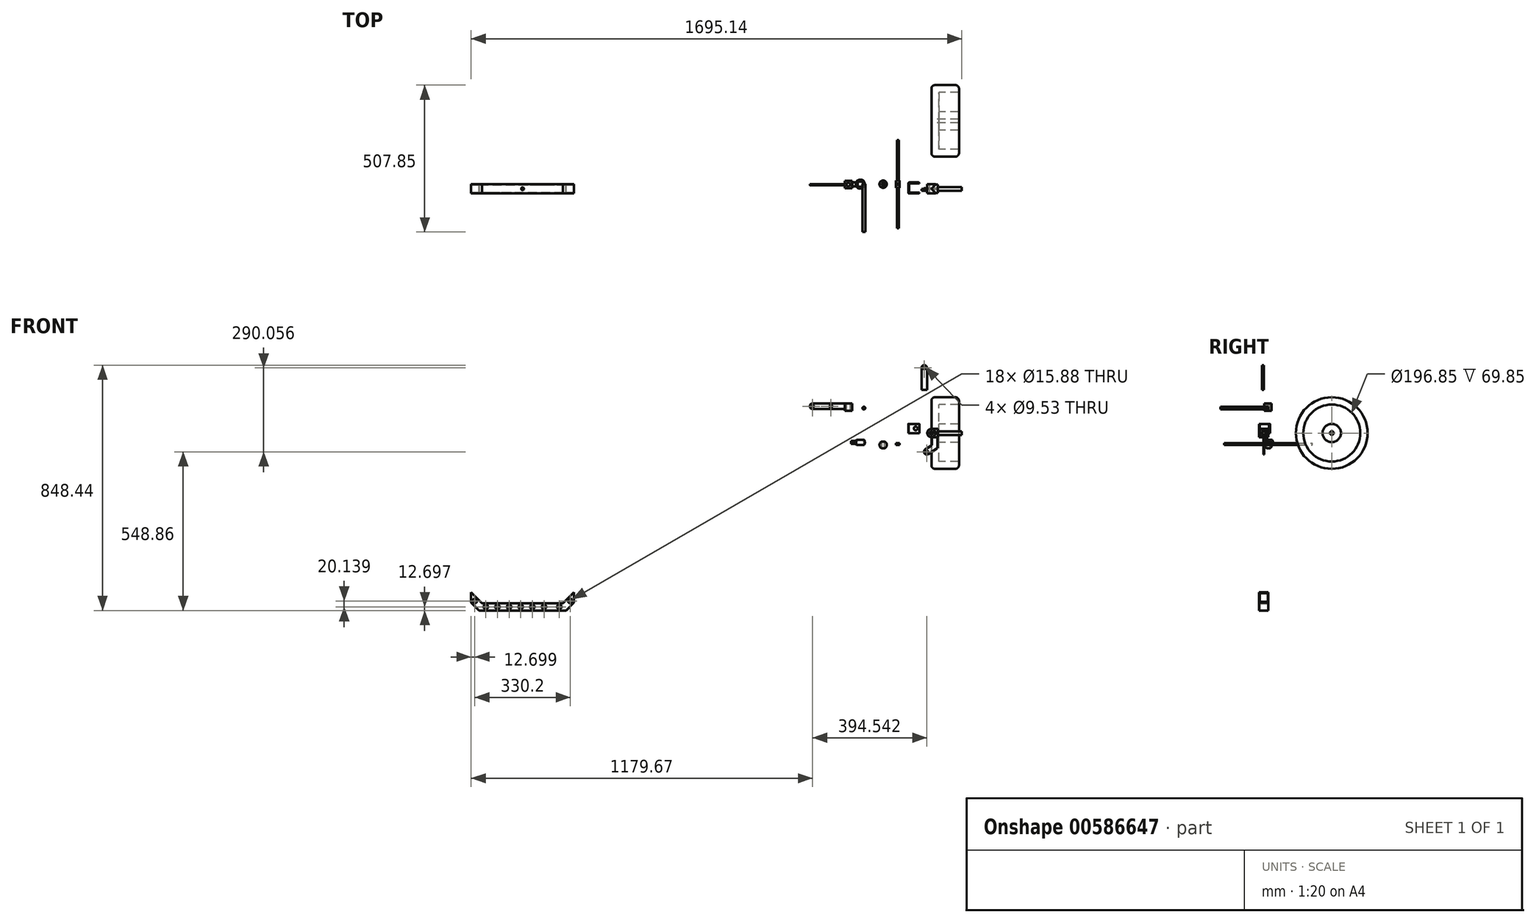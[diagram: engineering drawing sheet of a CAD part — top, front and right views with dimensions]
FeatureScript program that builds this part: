
annotation { "Feature Type Name" : "Feature", "Feature Type Description" : "" }
export const myFeature = defineFeature(function(context is Context, id is Id, definition is map)
    precondition{}
    {
        {
            var Q0;
            Q0=qCreatedBy(makeId("Front.planeOp"),FACE);
            var sketch = newSketch(context, id + "F0", { "sketchPlane" : qUnion([Q0])});
            skCircle(sketch, "E0", {"center": v(0, 0) * mm, "radius": 14.29 * mm});
            skCircle(sketch, "E1", {"center": v(0, 0) * mm, "radius": 6.35 * mm});
            skSolve(sketch);
        }
        {
            var Q0;
            Q0=makeQuery(id+"F0.imprint","IMPRINT",FACE,{"disambiguationData":[TD([[makeQuery(id+"F0.imprint","IMPRINT",EDGE,{"derivedFrom":sQuery(id+"F0.wireOp",EDGE,"E0")}),1.0]])]});
            extrude(context, id + "F1", {"entities" : qUnion([Q0]), "depth" : 31.75 * mm, "offsetDistance" : 25.4 * mm});
        }
        {
            var Q0;
            Q0=qCreatedBy(makeId("Right.planeOp"),FACE);
            cPlane(context, id + "F2", {"entities" : qUnion([Q0]), "cplaneType" : CPlaneType.OFFSET, "offset" : 22.22 * mm, "width" : 152.4 * mm, "height" : 152.4 * mm});
        }
        {
            var Q0;
            Q0=qCreatedBy(id+"F2.planeOp",FACE);
            var sketch = newSketch(context, id + "F3", { "sketchPlane" : qUnion([Q0])});
            skCircle(sketch, "E2", {"center": v(-15.88, 0) * mm, "radius": 14.29 * mm});
            skSolve(sketch);
        }
        {
            var Q0;
            Q0=makeQuery(id+"F3.imprint","IMPRINT",FACE,{"disambiguationData":[TD([[makeQuery(id+"F3.imprint","IMPRINT",EDGE,{"derivedFrom":sQuery(id+"F3.wireOp",EDGE,"E2")}),1.0]])]});
            extrude(context, id + "F4", {"entities" : qUnion([Q0]), "operationType" : NewBodyOperationType.ADD, "endBound" : BoundingType.UP_TO_NEXT, "oppositeDirection" : true, "depth" : 25.4 * mm, "offsetDistance" : 25.4 * mm});
        }
        {
            var Q0;
            Q0=makeQuery(id+"F4.opExtrude","CAP_FACE",FACE,{"disambiguationData":[OSD([sQuery(id+"F3.wireOp",EDGE,"E2")])],"isStart":true});
            var sketch = newSketch(context, id + "F5", { "sketchPlane" : qUnion([Q0])});
            skCircle(sketch, "E3", {"center": v(-15.88, 0) * mm, "radius": 6.35 * mm});
            skSolve(sketch);
        }
        {
            var Q0;
            Q0=makeQuery(id+"F5.imprint","IMPRINT",FACE,{"disambiguationData":[TD([[makeQuery(id+"F5.imprint","IMPRINT",EDGE,{"derivedFrom":sQuery(id+"F5.wireOp",EDGE,"E3")}),1.0]])]});
            extrude(context, id + "F6", {"entities" : qUnion([Q0]), "operationType" : NewBodyOperationType.ADD, "depth" : 82.55 * mm, "offsetDistance" : 25.4 * mm});
        }
        {
            var Q0;
            Q0=qCreatedBy(makeId("Top.planeOp"),FACE);
            var sketch = newSketch(context, id + "F7", { "sketchPlane" : qUnion([Q0])});
            skLineSegment(sketch, "E4.bottom", {"start": v(-76.48, 5.78) * mm, "end": v(-44.73, 5.78) * mm});
            skLineSegment(sketch, "E4.top", {"start": v(-76.48, -32.32) * mm, "end": v(-44.73, -32.32) * mm});
            skLineSegment(sketch, "E4.left", {"start": v(-79.65, 2.6) * mm, "end": v(-79.65, -29.15) * mm});
            skLineSegment(sketch, "E4.right", {"start": v(-41.55, 2.6) * mm, "end": v(-41.55, -29.15) * mm});
            skPoint(sketch, "E5.visualSharp", {"position": v(-41.55, 5.78) * mm});
            skArc(sketch, "E5.filletArc", {"start": v(-41.55, 2.6) * mm, "mid": v(-42.48, 4.85) * mm, "end": v(-44.73, 5.78) * mm});
            skPoint(sketch, "E6.visualSharp", {"position": v(-41.55, -32.32) * mm});
            skArc(sketch, "E6.filletArc", {"start": v(-44.73, -32.32) * mm, "mid": v(-42.48, -31.4) * mm, "end": v(-41.55, -29.15) * mm});
            skPoint(sketch, "E7.visualSharp", {"position": v(-79.65, -32.32) * mm});
            skArc(sketch, "E7.filletArc", {"start": v(-79.65, -29.15) * mm, "mid": v(-78.72, -31.4) * mm, "end": v(-76.48, -32.32) * mm});
            skPoint(sketch, "E8.visualSharp", {"position": v(-79.65, 5.78) * mm});
            skArc(sketch, "E8.filletArc", {"start": v(-76.48, 5.78) * mm, "mid": v(-78.72, 4.85) * mm, "end": v(-79.65, 2.6) * mm});
            skLineSegment(sketch, "E9.0", {"start": v(-76.48, 2.73) * mm, "end": v(-44.73, 2.73) * mm});
            skArc(sketch, "E9.1", {"start": v(-44.6, 2.6) * mm, "mid": v(-44.64, 2.7) * mm, "end": v(-44.73, 2.73) * mm});
            skArc(sketch, "E9.2", {"start": v(-76.48, 2.73) * mm, "mid": v(-76.57, 2.7) * mm, "end": v(-76.6, 2.6) * mm});
            skLineSegment(sketch, "E9.3", {"start": v(-44.6, 2.6) * mm, "end": v(-44.6, -29.15) * mm});
            skLineSegment(sketch, "E9.4", {"start": v(-76.6, 2.6) * mm, "end": v(-76.6, -29.15) * mm});
            skArc(sketch, "E9.5", {"start": v(-76.6, -29.15) * mm, "mid": v(-76.57, -29.24) * mm, "end": v(-76.48, -29.28) * mm});
            skLineSegment(sketch, "E9.6", {"start": v(-76.48, -29.28) * mm, "end": v(-44.73, -29.28) * mm});
            skArc(sketch, "E9.7", {"start": v(-44.73, -29.28) * mm, "mid": v(-44.64, -29.24) * mm, "end": v(-44.6, -29.15) * mm});
            skSolve(sketch);
        }
        {
            var Q0;
            Q0=makeQuery(id+"F7.imprint","IMPRINT",FACE,{"disambiguationData":[TD([[makeQuery(id+"F7.imprint","IMPRINT",EDGE,{"derivedFrom":sQuery(id+"F7.wireOp",EDGE,"E4.bottom")}),-1.0]])]});
            extrude(context, id + "F8", {"entities" : qUnion([Q0]), "depth" : 31.75 * mm, "offsetDistance" : 25.4 * mm});
        }
        {
            var Q0;
            Q0=makeQuery(id+"F8.opExtrude","CAP_FACE",FACE,{"disambiguationData":[OSD([sQuery(id+"F7.wireOp",EDGE,"E4.bottom"),sQuery(id+"F7.wireOp",EDGE,"E4.top"),sQuery(id+"F7.wireOp",EDGE,"E4.left"),sQuery(id+"F7.wireOp",EDGE,"E4.right"),sQuery(id+"F7.wireOp",EDGE,"E5.filletArc"),sQuery(id+"F7.wireOp",EDGE,"E6.filletArc"),sQuery(id+"F7.wireOp",EDGE,"E7.filletArc"),sQuery(id+"F7.wireOp",EDGE,"E8.filletArc"),sQuery(id+"F7.wireOp",EDGE,"E9.0"),sQuery(id+"F7.wireOp",EDGE,"E9.1"),sQuery(id+"F7.wireOp",EDGE,"E9.2"),sQuery(id+"F7.wireOp",EDGE,"E9.3"),sQuery(id+"F7.wireOp",EDGE,"E9.4"),sQuery(id+"F7.wireOp",EDGE,"E9.5"),sQuery(id+"F7.wireOp",EDGE,"E9.6"),sQuery(id+"F7.wireOp",EDGE,"E9.7")])],"isStart":false});
            var sketch = newSketch(context, id + "F9", { "sketchPlane" : qUnion([Q0])});
            skLineSegment(sketch, "E10.bottom", {"start": v(-44.73, 2.73) * mm, "end": v(-41.56, 2.73) * mm});
            skLineSegment(sketch, "E10.top", {"start": v(-44.73, -29.28) * mm, "end": v(-41.56, -29.28) * mm});
            skLineSegment(sketch, "E10.left", {"start": v(-44.73, 2.73) * mm, "end": v(-44.73, -29.28) * mm});
            skLineSegment(sketch, "E10.right", {"start": v(-41.56, 2.73) * mm, "end": v(-41.56, -29.28) * mm});
            skSolve(sketch);
        }
        {
            var Q0;
            Q0=makeQuery(id+"F9.imprint","IMPRINT",FACE,{"disambiguationData":[TD([[makeQuery(id+"F9.imprint","IMPRINT",EDGE,{"derivedFrom":sQuery(id+"F9.wireOp",EDGE,"E10.bottom")}),-1.0]])]});
            extrude(context, id + "F10", {"entities" : qUnion([Q0]), "operationType" : NewBodyOperationType.REMOVE, "endBound" : BoundingType.UP_TO_NEXT, "oppositeDirection" : true, "depth" : 25.4 * mm, "offsetDistance" : 25.4 * mm});
        }
        {
            var Q0;
            Q0=makeQuery(id+"F8.opExtrude","SWEPT_FACE",FACE,{"disambiguationData":[OSD([sQuery(id+"F7.wireOp",EDGE,"E4.bottom")])]});
            var sketch = newSketch(context, id + "F11", { "sketchPlane" : qUnion([Q0])});
            skCircle(sketch, "E11", {"center": v(54.26, 15.87) * mm, "radius": 6.35 * mm});
            skSolve(sketch);
        }
        {
            var Q0;
            Q0=makeQuery(id+"F11.imprint","IMPRINT",FACE,{"disambiguationData":[TD([[makeQuery(id+"F11.imprint","IMPRINT",EDGE,{"derivedFrom":sQuery(id+"F11.wireOp",EDGE,"E11")}),1.0]])]});
            var Q1;
            Q1=makeQuery(id+"F8.opExtrude","SWEPT_FACE",FACE,{"disambiguationData":[OSD([sQuery(id+"F7.wireOp",EDGE,"E4.top")])]});
            extrude(context, id + "F12", {"entities" : qUnion([Q0]), "operationType" : NewBodyOperationType.REMOVE, "endBound" : BoundingType.UP_TO_SURFACE, "oppositeDirection" : true, "depth" : 25.4 * mm, "endBoundEntityFace" : qUnion([Q1]), "offsetDistance" : 25.4 * mm});
        }
        {
            var Q0;
            Q0=qCreatedBy(makeId("Right.planeOp"),FACE);
            var sketch = newSketch(context, id + "F13", { "sketchPlane" : qUnion([Q0])});
            skCircle(sketch, "E12", {"center": v(218.92, 0) * mm, "radius": 123.83 * mm});
            skCircle(sketch, "E13", {"center": v(218.92, 0) * mm, "radius": 6.35 * mm});
            skSolve(sketch);
        }
        {
            var Q0;
            Q0=makeQuery(id+"F13.imprint","IMPRINT",FACE,{"disambiguationData":[TD([[makeQuery(id+"F13.imprint","IMPRINT",EDGE,{"derivedFrom":sQuery(id+"F13.wireOp",EDGE,"E12")}),1.0]])]});
            extrude(context, id + "F14", {"entities" : qUnion([Q0]), "depth" : 95.25 * mm, "offsetDistance" : 25.4 * mm});
        }
        {
            var Q0;
            Q0=makeQuery(id+"F14.opExtrude","CAP_EDGE",EDGE,{"disambiguationData":[OSD([sQuery(id+"F13.wireOp",EDGE,"E12")])],"isStart":false});
            var Q1;
            Q1=makeQuery(id+"F14.opExtrude","CAP_EDGE",EDGE,{"disambiguationData":[OSD([sQuery(id+"F13.wireOp",EDGE,"E12")])],"isStart":true});
            fillet(context, id + "F15", {"entities" : qUnion([Q0, Q1]), "radius" : 12.7 * mm, "tangentPropagation" : true, "allowEdgeOverflow" : false});
        }
        {
            var Q0;
            Q0=qCreatedBy(makeId("Front.planeOp"),FACE);
            cPlane(context, id + "F16", {"entities" : qUnion([Q0]), "cplaneType" : CPlaneType.OFFSET, "offset" : 15.88 * mm, "width" : 152.4 * mm, "height" : 152.4 * mm});
        }
        {
            var Q0;
            Q0=qCreatedBy(id+"F16.planeOp",FACE);
            var sketch = newSketch(context, id + "F17", { "sketchPlane" : qUnion([Q0])});
            skLineSegment(sketch, "E14", {"start": v(1.9, -13.97) * mm, "end": v(20.96, -13.97) * mm});
            skLineSegment(sketch, "E15", {"start": v(20.95, -13.97) * mm, "end": v(20.96, -52.07) * mm});
            skLineSegment(sketch, "E16", {"start": v(1.9, -13.97) * mm, "end": v(1.9, -41.72) * mm});
            skLineSegment(sketch, "E17", {"start": v(1.9, -41.72) * mm, "end": v(-21.33, -56.78) * mm});
            skLineSegment(sketch, "E18", {"start": v(20.96, -52.07) * mm, "end": v(-10.97, -72.76) * mm});
            skArc(sketch, "E19", {"start": v(-21.33, -56.78) * mm, "mid": v(-24.14, -69.95) * mm, "end": v(-10.97, -72.76) * mm});
            skCircle(sketch, "E20", {"center": v(-16.15, -64.77) * mm, "radius": 4.76 * mm});
            skLineSegment(sketch, "E21", {"start": v(0, 0) * mm, "end": v(-16.15, -64.77) * mm, "construction": true});
            skSolve(sketch);
        }
        {
            var Q0;
            Q0=makeQuery(id+"F17.imprint","IMPRINT",FACE,{"disambiguationData":[TD([[makeQuery(id+"F17.imprint","IMPRINT",EDGE,{"derivedFrom":sQuery(id+"F17.wireOp",EDGE,"E14")}),-1.0]])]});
            extrude(context, id + "F18", {"entities" : qUnion([Q0]), "operationType" : NewBodyOperationType.ADD, "depth" : 3.18 * mm, "offsetDistance" : 25.4 * mm, "symmetric" : true});
        }
        {
            var Q0;
            Q0=makeQuery(id+"F18.opExtrude","SWEPT_EDGE",EDGE,{"disambiguationData":[OSD([sQuery(id+"F17.wireOp",EDGE,"E15"),sQuery(id+"F17.wireOp",EDGE,"E18")])]});
            var Q1;
            Q1=makeQuery(id+"F18.opExtrude","SWEPT_EDGE",EDGE,{"disambiguationData":[OSD([sQuery(id+"F17.wireOp",EDGE,"E16"),sQuery(id+"F17.wireOp",EDGE,"E17")])]});
            fillet(context, id + "F19", {"entities" : qUnion([Q0, Q1]), "radius" : 6.35 * mm, "tangentPropagation" : true, "allowEdgeOverflow" : false});
        }
        {
            var Q0;
            Q0=qCreatedBy(makeId("Front.planeOp"),FACE);
            var sketch = newSketch(context, id + "F20", { "sketchPlane" : qUnion([Q0])});
            skLineSegment(sketch, "E22", {"start": v(-1590.36, -586.05) * mm, "end": v(-1562.78, -613.63) * mm});
            skLineSegment(sketch, "E23", {"start": v(-1562.78, -613.63) * mm, "end": v(-1262.34, -613.63) * mm});
            skLineSegment(sketch, "E24", {"start": v(-1262.34, -613.63) * mm, "end": v(-1234.76, -586.05) * mm});
            skLineSegment(sketch, "E25", {"start": v(-1234.76, -550.13) * mm, "end": v(-1272.86, -588.23) * mm});
            skLineSegment(sketch, "E26", {"start": v(-1272.86, -588.23) * mm, "end": v(-1552.26, -588.23) * mm});
            skLineSegment(sketch, "E27", {"start": v(-1552.26, -588.23) * mm, "end": v(-1590.36, -550.13) * mm});
            skLineSegment(sketch, "E28", {"start": v(-1590.36, -586.05) * mm, "end": v(-1590.36, -550.13) * mm});
            skLineSegment(sketch, "E29", {"start": v(-1234.76, -586.05) * mm, "end": v(-1234.76, -550.13) * mm});
            skSolve(sketch);
        }
        {
            var Q0;
            Q0=makeQuery(id+"F20.imprint","IMPRINT",FACE,{"disambiguationData":[TD([[makeQuery(id+"F20.imprint","IMPRINT",EDGE,{"derivedFrom":sQuery(id+"F20.wireOp",EDGE,"E22")}),1.0]])]});
            extrude(context, id + "F21", {"entities" : qUnion([Q0]), "depth" : 31.75 * mm, "offsetDistance" : 25.4 * mm});
        }
        {
            var Q0;
            Q0=makeQuery(id+"F21.opExtrude","SWEPT_FACE",FACE,{"disambiguationData":[OSD([sQuery(id+"F20.wireOp",EDGE,"E29")])]});
            shell(context, id + "F22", {"entities" : qUnion([Q0]), "thickness" : 2.1 * mm});
        }
        {
            var Q0;
            Q0=makeQuery(id+"F21.opExtrude","CAP_FACE",FACE,{"disambiguationData":[OSD([sQuery(id+"F20.wireOp",EDGE,"E22"),sQuery(id+"F20.wireOp",EDGE,"E23"),sQuery(id+"F20.wireOp",EDGE,"E24"),sQuery(id+"F20.wireOp",EDGE,"E25"),sQuery(id+"F20.wireOp",EDGE,"E26"),sQuery(id+"F20.wireOp",EDGE,"E27"),sQuery(id+"F20.wireOp",EDGE,"E28"),sQuery(id+"F20.wireOp",EDGE,"E29")])],"isStart":false});
            var sketch = newSketch(context, id + "F23", { "sketchPlane" : qUnion([Q0])});
            skCircle(sketch, "E30", {"center": v(-1577.66, -580.8) * mm, "radius": 7.94 * mm});
            skCircle(sketch, "E31", {"center": v(-1539.56, -600.93) * mm, "radius": 7.94 * mm});
            skCircle(sketch, "E32", {"center": v(-1499.35, -600.93) * mm, "radius": 7.94 * mm});
            skCircle(sketch, "E33", {"center": v(-1459.14, -600.93) * mm, "radius": 7.94 * mm});
            skCircle(sketch, "E34", {"center": v(-1418.94, -600.93) * mm, "radius": 7.94 * mm});
            skCircle(sketch, "E35", {"center": v(-1378.73, -600.93) * mm, "radius": 7.94 * mm});
            skCircle(sketch, "E36", {"center": v(-1338.52, -600.93) * mm, "radius": 7.94 * mm});
            skCircle(sketch, "E37", {"center": v(-1285.56, -600.93) * mm, "radius": 7.94 * mm});
            skCircle(sketch, "E38", {"center": v(-1247.46, -580.8) * mm, "radius": 7.94 * mm});
            skLineSegment(sketch, "E39", {"start": v(-1539.56, -600.93) * mm, "end": v(-1285.56, -600.93) * mm, "construction": true});
            skSolve(sketch);
        }
        {
            var Q0;
            Q0=makeQuery(id+"F23.imprint","IMPRINT",FACE,{"disambiguationData":[TD([[makeQuery(id+"F23.imprint","IMPRINT",EDGE,{"derivedFrom":sQuery(id+"F23.wireOp",EDGE,"E30")}),1.0]])]});
            var Q1;
            Q1=makeQuery(id+"F23.imprint","IMPRINT",FACE,{"disambiguationData":[TD([[makeQuery(id+"F23.imprint","IMPRINT",EDGE,{"derivedFrom":sQuery(id+"F23.wireOp",EDGE,"E31")}),1.0]])]});
            var Q2;
            Q2=makeQuery(id+"F23.imprint","IMPRINT",FACE,{"disambiguationData":[TD([[makeQuery(id+"F23.imprint","IMPRINT",EDGE,{"derivedFrom":sQuery(id+"F23.wireOp",EDGE,"E32")}),1.0]])]});
            var Q3;
            Q3=makeQuery(id+"F23.imprint","IMPRINT",FACE,{"disambiguationData":[TD([[makeQuery(id+"F23.imprint","IMPRINT",EDGE,{"derivedFrom":sQuery(id+"F23.wireOp",EDGE,"E33")}),1.0]])]});
            var Q4;
            Q4=makeQuery(id+"F23.imprint","IMPRINT",FACE,{"disambiguationData":[TD([[makeQuery(id+"F23.imprint","IMPRINT",EDGE,{"derivedFrom":sQuery(id+"F23.wireOp",EDGE,"E34")}),1.0]])]});
            var Q5;
            Q5=makeQuery(id+"F23.imprint","IMPRINT",FACE,{"disambiguationData":[TD([[makeQuery(id+"F23.imprint","IMPRINT",EDGE,{"derivedFrom":sQuery(id+"F23.wireOp",EDGE,"E35")}),1.0]])]});
            var Q6;
            Q6=makeQuery(id+"F23.imprint","IMPRINT",FACE,{"disambiguationData":[TD([[makeQuery(id+"F23.imprint","IMPRINT",EDGE,{"derivedFrom":sQuery(id+"F23.wireOp",EDGE,"E36")}),1.0]])]});
            var Q7;
            Q7=makeQuery(id+"F23.imprint","IMPRINT",FACE,{"disambiguationData":[TD([[makeQuery(id+"F23.imprint","IMPRINT",EDGE,{"derivedFrom":sQuery(id+"F23.wireOp",EDGE,"E37")}),1.0]])]});
            var Q8;
            Q8=makeQuery(id+"F23.imprint","IMPRINT",FACE,{"disambiguationData":[TD([[makeQuery(id+"F23.imprint","IMPRINT",EDGE,{"derivedFrom":sQuery(id+"F23.wireOp",EDGE,"E38")}),1.0]])]});
            var Q9;
            Q9=makeQuery(id+"F21.opExtrude","CAP_FACE",FACE,{"disambiguationData":[OSD([sQuery(id+"F20.wireOp",EDGE,"E22"),sQuery(id+"F20.wireOp",EDGE,"E23"),sQuery(id+"F20.wireOp",EDGE,"E24"),sQuery(id+"F20.wireOp",EDGE,"E25"),sQuery(id+"F20.wireOp",EDGE,"E26"),sQuery(id+"F20.wireOp",EDGE,"E27"),sQuery(id+"F20.wireOp",EDGE,"E28"),sQuery(id+"F20.wireOp",EDGE,"E29")])],"isStart":true});
            extrude(context, id + "F24", {"entities" : qUnion([Q0, Q1, Q2, Q3, Q4, Q5, Q6, Q7, Q8]), "operationType" : NewBodyOperationType.REMOVE, "endBound" : BoundingType.UP_TO_SURFACE, "oppositeDirection" : true, "depth" : 25.4 * mm, "endBoundEntityFace" : qUnion([Q9]), "offsetDistance" : 25.4 * mm});
        }
        {
            var Q0;
            Q0=makeQuery(id+"F14.opExtrude","CAP_FACE",FACE,{"disambiguationData":[OSD([sQuery(id+"F13.wireOp",EDGE,"E12"),sQuery(id+"F13.wireOp",EDGE,"E13")])],"isStart":false});
            shell(context, id + "F25", {"entities" : qUnion([Q0]), "thickness" : 25.4 * mm});
        }
        {
            var Q0;
            Q0=qCreatedBy(makeId("Front.planeOp"),FACE);
            var sketch = newSketch(context, id + "F26", { "sketchPlane" : qUnion([Q0])});
            skLineSegment(sketch, "E40.bottom", {"start": v(-410.7, 102.22) * mm, "end": v(-283.7, 102.22) * mm});
            skLineSegment(sketch, "E40.top", {"start": v(-410.7, 83.17) * mm, "end": v(-283.7, 83.17) * mm});
            skLineSegment(sketch, "E40.left", {"start": v(-410.7, 102.22) * mm, "end": v(-410.7, 83.17) * mm, "construction": true});
            skLineSegment(sketch, "E40.right", {"start": v(-283.7, 102.22) * mm, "end": v(-283.7, 83.17) * mm, "construction": true});
            skArc(sketch, "E41", {"start": v(-410.7, 102.22) * mm, "mid": v(-420.22, 92.7) * mm, "end": v(-410.7, 83.17) * mm});
            skArc(sketch, "E42", {"start": v(-283.7, 83.17) * mm, "mid": v(-274.17, 92.7) * mm, "end": v(-283.7, 102.22) * mm});
            skCircle(sketch, "E43", {"center": v(-410.7, 92.7) * mm, "radius": 4.76 * mm});
            skCircle(sketch, "E44", {"center": v(-283.7, 92.7) * mm, "radius": 4.76 * mm});
            skCircle(sketch, "E45", {"center": v(-347.2, 92.7) * mm, "radius": 4.76 * mm});
            skLineSegment(sketch, "E46", {"start": v(-410.7, 92.7) * mm, "end": v(-283.7, 92.7) * mm, "construction": true});
            skSolve(sketch);
        }
        {
            var Q0;
            Q0=makeQuery(id+"F26.imprint","IMPRINT",FACE,{"disambiguationData":[TD([[makeQuery(id+"F26.imprint","IMPRINT",EDGE,{"derivedFrom":sQuery(id+"F26.wireOp",EDGE,"E40.bottom")}),-1.0]])]});
            extrude(context, id + "F27", {"entities" : qUnion([Q0]), "depth" : 3.17 * mm, "offsetDistance" : 25.4 * mm});
        }
        {
            var Q0;
            Q0=makeQuery(id+"F21.opExtrude","SWEPT_FACE",FACE,{"disambiguationData":[OSD([sQuery(id+"F20.wireOp",EDGE,"E26")])]});
            var sketch = newSketch(context, id + "F28", { "sketchPlane" : qUnion([Q0])});
            skCircle(sketch, "E47", {"center": v(-1412.56, -15.88) * mm, "radius": 4.76 * mm});
            skLineSegment(sketch, "E48", {"start": v(-1552.26, -15.88) * mm, "end": v(-1272.86, -15.88) * mm, "construction": true});
            skSolve(sketch);
        }
        {
            var Q0;
            Q0=makeQuery(id+"F28.imprint","IMPRINT",FACE,{"disambiguationData":[TD([[makeQuery(id+"F28.imprint","IMPRINT",EDGE,{"derivedFrom":sQuery(id+"F28.wireOp",EDGE,"E47")}),1.0]])]});
            extrude(context, id + "F29", {"entities" : qUnion([Q0]), "operationType" : NewBodyOperationType.REMOVE, "endBound" : BoundingType.UP_TO_NEXT, "oppositeDirection" : true, "depth" : 25.4 * mm, "offsetDistance" : 25.4 * mm});
        }
        {
            var Q0;
            Q0=qCreatedBy(makeId("Front.planeOp"),FACE);
            var sketch = newSketch(context, id + "F30", { "sketchPlane" : qUnion([Q0])});
            skArc(sketch, "E49", {"start": v(-171.5, -29.27) * mm, "mid": v(-179.44, -41.04) * mm, "end": v(-171.5, -52.82) * mm});
            skLineSegment(sketch, "E50", {"start": v(-166.74, -28.34) * mm, "end": v(-166.74, -53.74) * mm, "construction": true});
            skLineSegment(sketch, "E51", {"start": v(-171.5, -29.27) * mm, "end": v(-171.5, -52.82) * mm});
            skSolve(sketch);
        }
        {
            var Q0;
            Q0=makeQuery(id+"F30.imprint","IMPRINT",FACE,{"disambiguationData":[TD([[makeQuery(id+"F30.imprint","IMPRINT",EDGE,{"derivedFrom":sQuery(id+"F30.wireOp",EDGE,"E49")}),1.0]])]});
            var Q1;
            Q1=sQuery(id+"F30.wireOp",EDGE,"E50");
            revolve(context, id + "F31", {"entities" : qUnion([Q0]), "axis" : qUnion([Q1]), "revolveType" : RevolveType.FULL});
        }
        {
            var Q0;
            Q0=qCreatedBy(makeId("Front.planeOp"),FACE);
            var sketch = newSketch(context, id + "F32", { "sketchPlane" : qUnion([Q0])});
            skLineSegment(sketch, "E52", {"start": v(-245.74, -9.54) * mm, "end": v(-245.74, -54.1) * mm, "construction": true});
            skArc(sketch, "E53", {"start": v(-255.26, -24.1) * mm, "mid": v(-258.44, -32.5) * mm, "end": v(-255.26, -40.9) * mm});
            skArc(sketch, "E54.0", {"start": v(-259.2, -24.1) * mm, "mid": v(-261.61, -32.5) * mm, "end": v(-259.2, -40.9) * mm});
            skLineSegment(sketch, "E55", {"start": v(-255.26, -40.9) * mm, "end": v(-259.2, -40.9) * mm});
            skLineSegment(sketch, "E56", {"start": v(-255.26, -24.1) * mm, "end": v(-259.2, -24.1) * mm});
            skSolve(sketch);
        }
        {
            var Q0;
            Q0=makeQuery(id+"F32.imprint","IMPRINT",FACE,{"disambiguationData":[TD([[makeQuery(id+"F32.imprint","IMPRINT",EDGE,{"derivedFrom":sQuery(id+"F32.wireOp",EDGE,"E53")}),-1.0]])]});
            var Q1;
            Q1=sQuery(id+"F32.wireOp",EDGE,"E52");
            revolve(context, id + "F33", {"entities" : qUnion([Q0]), "axis" : qUnion([Q1]), "revolveType" : RevolveType.FULL});
        }
        {
            var Q0;
            Q0=qCreatedBy(makeId("Front.planeOp"),FACE);
            var sketch = newSketch(context, id + "F34", { "sketchPlane" : qUnion([Q0])});
            skLineSegment(sketch, "E57.bottom", {"start": v(-259.06, -37.25) * mm, "end": v(-278.11, -37.25) * mm});
            skLineSegment(sketch, "E57.top", {"start": v(-259.06, -27.73) * mm, "end": v(-278.11, -27.73) * mm});
            skLineSegment(sketch, "E57.left", {"start": v(-259.06, -37.25) * mm, "end": v(-259.06, -27.73) * mm});
            skLineSegment(sketch, "E57.right", {"start": v(-278.11, -37.25) * mm, "end": v(-278.11, -27.73) * mm});
            skSolve(sketch);
        }
        {
            var Q0;
            Q0=makeQuery(id+"F34.imprint","IMPRINT",FACE,{"disambiguationData":[TD([[makeQuery(id+"F34.imprint","IMPRINT",EDGE,{"derivedFrom":sQuery(id+"F34.wireOp",EDGE,"E57.bottom")}),-1.0]])]});
            extrude(context, id + "F35", {"entities" : qUnion([Q0]), "operationType" : NewBodyOperationType.ADD, "depth" : 13.97 * mm, "offsetDistance" : 25.4 * mm, "symmetric" : true});
        }
        {
            var Q0;
            Q0=makeQuery(id+"F35.opExtrude","CAP_EDGE",EDGE,{"disambiguationData":[OSD([sQuery(id+"F34.wireOp",EDGE,"E57.top")])],"isStart":false});
            var Q1;
            Q1=makeQuery(id+"F35.opExtrude","CAP_EDGE",EDGE,{"disambiguationData":[OSD([sQuery(id+"F34.wireOp",EDGE,"E57.top")])],"isStart":true});
            var Q2;
            Q2=makeQuery(id+"F35.opExtrude","CAP_EDGE",EDGE,{"disambiguationData":[OSD([sQuery(id+"F34.wireOp",EDGE,"E57.bottom")])],"isStart":false});
            var Q3;
            Q3=makeQuery(id+"F35.opExtrude","CAP_EDGE",EDGE,{"disambiguationData":[OSD([sQuery(id+"F34.wireOp",EDGE,"E57.bottom")])],"isStart":true});
            fillet(context, id + "F36", {"entities" : qUnion([Q0, Q1, Q2, Q3]), "radius" : 5.08 * mm, "tangentPropagation" : true, "allowEdgeOverflow" : false});
        }
        {
            var Q0;
            Q0=makeQuery(id+"F35.opExtrude","SWEPT_FACE",FACE,{"disambiguationData":[OSD([sQuery(id+"F34.wireOp",EDGE,"E57.right")])]});
            var sketch = newSketch(context, id + "F37", { "sketchPlane" : qUnion([Q0])});
            skLineSegment(sketch, "E58", {"start": v(0, -27.73) * mm, "end": v(0, -37.25) * mm, "construction": true});
            skCircle(sketch, "E59", {"center": v(0, -32.5) * mm, "radius": 3.18 * mm});
            skSolve(sketch);
        }
        {
            var Q0;
            Q0=makeQuery(id+"F37.imprint","IMPRINT",FACE,{"disambiguationData":[TD([[makeQuery(id+"F37.imprint","IMPRINT",EDGE,{"derivedFrom":sQuery(id+"F37.wireOp",EDGE,"E59")}),1.0]])]});
            extrude(context, id + "F38", {"entities" : qUnion([Q0]), "operationType" : NewBodyOperationType.REMOVE, "oppositeDirection" : true, "depth" : 6.35 * mm, "offsetDistance" : 25.4 * mm});
        }
        {
            var Q0;
            Q0=qCreatedBy(makeId("Front.planeOp"),FACE);
            var sketch = newSketch(context, id + "F39", { "sketchPlane" : qUnion([Q0])});
            skCircle(sketch, "E60", {"center": v(-115.73, -37.52) * mm, "radius": 3.18 * mm});
            skSolve(sketch);
        }
        {
            var Q0;
            Q0=makeQuery(id+"F39.imprint","IMPRINT",FACE,{"disambiguationData":[TD([[makeQuery(id+"F39.imprint","IMPRINT",EDGE,{"derivedFrom":sQuery(id+"F39.wireOp",EDGE,"E60")}),1.0]])]});
            extrude(context, id + "F40", {"entities" : qUnion([Q0]), "depth" : 304.8 * mm, "offsetDistance" : 25.4 * mm, "symmetric" : true});
        }
        {
            var Q0;
            Q0=qCreatedBy(makeId("Front.planeOp"),FACE);
            var sketch = newSketch(context, id + "F41", { "sketchPlane" : qUnion([Q0])});
            skCircle(sketch, "E61.0.0", {"center": v(-115.73, -37.52) * mm, "radius": 3.18 * mm});
            skLineSegment(sketch, "E62.bottom", {"start": v(-122.08, -34.35) * mm, "end": v(-109.38, -34.35) * mm});
            skLineSegment(sketch, "E62.top", {"start": v(-122.08, -40.7) * mm, "end": v(-109.38, -40.7) * mm});
            skLineSegment(sketch, "E62.left", {"start": v(-122.08, -34.35) * mm, "end": v(-122.08, -40.7) * mm});
            skLineSegment(sketch, "E62.right", {"start": v(-109.38, -34.35) * mm, "end": v(-109.38, -40.7) * mm});
            skLineSegment(sketch, "E63", {"start": v(-122.08, -34.35) * mm, "end": v(-109.38, -40.7) * mm, "construction": true});
            skSolve(sketch);
        }
        {
            var Q0;
            {var subQ5=sQuery(id+"F41.wireOp",EDGE,"E62.left");Q0=makeQuery(id+"F41.imprint","IMPRINT",FACE,{"disambiguationData":[TD([[makeQuery(id+"F41.imprint","IMPRINT",EDGE,{"derivedFrom":subQ5}),1.0]])]});}
            var Q1;
            {var subQ5=sQuery(id+"F41.wireOp",EDGE,"E62.right");Q1=makeQuery(id+"F41.imprint","IMPRINT",FACE,{"disambiguationData":[TD([[makeQuery(id+"F41.imprint","IMPRINT",EDGE,{"derivedFrom":subQ5}),-1.0]])]});}
            extrude(context, id + "F42", {"entities" : qUnion([Q0, Q1]), "operationType" : NewBodyOperationType.ADD, "depth" : 25.4 * mm, "offsetDistance" : 25.4 * mm, "symmetric" : true});
        }
        {
            var Q0;
            {var subQ0=sQuery(id+"F41.wireOp",EDGE,"E62.bottom");Q0=makeQuery(id+"F42.boolean.opBoolean","MERGE",FACE,{"derivedFrom":[makeQuery(id+"F42.opExtrude","SWEPT_FACE",FACE,{"disambiguationData":[OSD([subQ0]),TDD([makeQuery(id+"F41.imprint","IMPRINT",EDGE,{"disambiguationData":[TD([[makeQuery(id+"F41.imprint","INTERSECT",VERTEX,{"derivedFrom":[subQ0,sQuery(id+"F41.wireOp",EDGE,"E62.left")]}),-1.0]])],"derivedFrom":subQ0})])]}),makeQuery(id+"F42.opExtrude","SWEPT_FACE",FACE,{"disambiguationData":[OSD([subQ0]),TDD([makeQuery(id+"F41.imprint","IMPRINT",EDGE,{"disambiguationData":[TD([[makeQuery(id+"F41.imprint","INTERSECT",VERTEX,{"derivedFrom":[subQ0,sQuery(id+"F41.wireOp",EDGE,"E62.right")]}),1.0]])],"derivedFrom":subQ0})])]})]});}
            var sketch = newSketch(context, id + "F43", { "sketchPlane" : qUnion([Q0])});
            skLineSegment(sketch, "E64", {"start": v(-122.08, 0) * mm, "end": v(-109.38, 0) * mm, "construction": true});
            skCircle(sketch, "E65", {"center": v(-115.73, 0) * mm, "radius": 3.18 * mm});
            skSolve(sketch);
        }
        {
            var Q0;
            Q0=makeQuery(id+"F43.imprint","IMPRINT",FACE,{"disambiguationData":[TD([[makeQuery(id+"F43.imprint","IMPRINT",EDGE,{"derivedFrom":sQuery(id+"F43.wireOp",EDGE,"E65")}),1.0]])]});
            var Q1;
            {var subQ0=sQuery(id+"F41.wireOp",EDGE,"E62.top");Q1=makeQuery(id+"F42.boolean.opBoolean","MERGE",FACE,{"derivedFrom":[makeQuery(id+"F42.opExtrude","SWEPT_FACE",FACE,{"disambiguationData":[OSD([subQ0]),TDD([makeQuery(id+"F41.imprint","IMPRINT",EDGE,{"disambiguationData":[TD([[makeQuery(id+"F41.imprint","INTERSECT",VERTEX,{"derivedFrom":[subQ0,sQuery(id+"F41.wireOp",EDGE,"E62.left")]}),-1.0]])],"derivedFrom":subQ0})])]}),makeQuery(id+"F42.opExtrude","SWEPT_FACE",FACE,{"disambiguationData":[OSD([subQ0]),TDD([makeQuery(id+"F41.imprint","IMPRINT",EDGE,{"disambiguationData":[TD([[makeQuery(id+"F41.imprint","INTERSECT",VERTEX,{"derivedFrom":[subQ0,sQuery(id+"F41.wireOp",EDGE,"E62.right")]}),1.0]])],"derivedFrom":subQ0})])]})]});}
            extrude(context, id + "F44", {"entities" : qUnion([Q0]), "operationType" : NewBodyOperationType.REMOVE, "endBound" : BoundingType.UP_TO_SURFACE, "oppositeDirection" : true, "depth" : 25.4 * mm, "endBoundEntityFace" : qUnion([Q1]), "offsetDistance" : 25.4 * mm});
        }
        {
            var Q0;
            Q0=qCreatedBy(id+"F16.planeOp",FACE);
            var sketch = newSketch(context, id + "F45", { "sketchPlane" : qUnion([Q0])});
            skLineSegment(sketch, "E66.bottom", {"start": v(-34.4, 225.29) * mm, "end": v(-15.36, 225.29) * mm, "construction": true});
            skLineSegment(sketch, "E66.top", {"start": v(-34.4, 149.09) * mm, "end": v(-15.36, 149.09) * mm});
            skLineSegment(sketch, "E66.left", {"start": v(-34.4, 225.29) * mm, "end": v(-34.4, 149.09) * mm});
            skLineSegment(sketch, "E66.right", {"start": v(-15.36, 225.29) * mm, "end": v(-15.36, 149.09) * mm});
            skArc(sketch, "E67", {"start": v(-15.36, 225.29) * mm, "mid": v(-24.88, 234.81) * mm, "end": v(-34.4, 225.29) * mm});
            skCircle(sketch, "E68", {"center": v(-24.88, 225.29) * mm, "radius": 4.76 * mm});
            skPoint(sketch, "E69.center.orphan", {"position": v(-24.88, 149.09) * mm});
            skSolve(sketch);
        }
        {
            var Q0;
            Q0=makeQuery(id+"F45.imprint","IMPRINT",FACE,{"disambiguationData":[TD([[makeQuery(id+"F45.imprint","IMPRINT",EDGE,{"derivedFrom":sQuery(id+"F45.wireOp",EDGE,"E66.top")}),1.0]])]});
            extrude(context, id + "F46", {"entities" : qUnion([Q0]), "depth" : 6.35 * mm, "offsetDistance" : 25.4 * mm});
        }
        {
            var Q0;
            Q0=qCreatedBy(makeId("Front.planeOp"),FACE);
            var sketch = newSketch(context, id + "F47", { "sketchPlane" : qUnion([Q0])});
            skCircle(sketch, "E70", {"center": v(-233.34, 86.07) * mm, "radius": 4.76 * mm});
            skSolve(sketch);
        }
        {
            var Q0;
            Q0=makeQuery(id+"F47.imprint","IMPRINT",FACE,{"disambiguationData":[TD([[makeQuery(id+"F47.imprint","IMPRINT",EDGE,{"derivedFrom":sQuery(id+"F47.wireOp",EDGE,"E70")}),1.0]])]});
            extrude(context, id + "F48", {"entities" : qUnion([Q0]), "depth" : 165.1 * mm, "offsetDistance" : 25.4 * mm});
        }
        {
            var Q0;
            Q0=makeQuery(id+"F27.opExtrude","SWEPT_FACE",FACE,{"disambiguationData":[OSD([sQuery(id+"F26.wireOp",EDGE,"E40.bottom")])]});
            var sketch = newSketch(context, id + "F49", { "sketchPlane" : qUnion([Q0])});
            skLineSegment(sketch, "E71.bottom", {"start": v(-274.17, -13.97) * mm, "end": v(-299.57, -13.97) * mm});
            skLineSegment(sketch, "E71.top", {"start": v(-274.17, 11.43) * mm, "end": v(-299.57, 11.43) * mm});
            skLineSegment(sketch, "E71.left", {"start": v(-274.17, -13.97) * mm, "end": v(-274.17, 11.43) * mm});
            skLineSegment(sketch, "E71.right", {"start": v(-299.57, -13.97) * mm, "end": v(-299.57, 11.43) * mm});
            skSolve(sketch);
        }
        {
            var Q0;
            {var subQ1=sQuery(id+"F49.wireOp",EDGE,"E71.bottom");Q0=makeQuery(id+"F49.imprint","IMPRINT",FACE,{"disambiguationData":[TD([[makeQuery(id+"F49.imprint","IMPRINT",EDGE,{"derivedFrom":subQ1}),-1.0]])]});}
            var Q1;
            {var subQ1=sQuery(id+"F26.wireOp",EDGE,"E40.bottom");var subQ6=makeQuery(id+"F27.opExtrude","SWEPT_EDGE",EDGE,{"disambiguationData":[OSD([subQ1,sQuery(id+"F26.wireOp",EDGE,"E42")])]});Q1=makeQuery(id+"F49.imprint","IMPRINT",FACE,{"disambiguationData":[TD([[makeQuery(id+"F49.imprint","IMPRINT",EDGE,{"derivedFrom":subQ6}),1.0]])]});}
            extrude(context, id + "F50", {"entities" : qUnion([Q0, Q1]), "operationType" : NewBodyOperationType.ADD, "oppositeDirection" : true, "depth" : 25.4 * mm, "offsetDistance" : 25.4 * mm});
        }
        {
            var Q0;
            Q0=makeQuery(id+"F50.boolean.opBoolean","MERGE",FACE,{"derivedFrom":[makeQuery(id+"F27.opExtrude","SWEPT_FACE",FACE,{"disambiguationData":[OSD([sQuery(id+"F26.wireOp",EDGE,"E40.bottom")])]}),makeQuery(id+"F50.opExtrude","CAP_FACE",FACE,{"disambiguationData":[OSD([sQuery(id+"F49.wireOp",EDGE,"E71.bottom"),sQuery(id+"F49.wireOp",EDGE,"E71.top"),sQuery(id+"F49.wireOp",EDGE,"E71.left"),sQuery(id+"F49.wireOp",EDGE,"E71.right")])],"isStart":true})]});
            var sketch = newSketch(context, id + "F51", { "sketchPlane" : qUnion([Q0])});
            skCircle(sketch, "E72", {"center": v(-286.87, -1.27) * mm, "radius": 6.35 * mm});
            skSolve(sketch);
        }
        {
            var Q0;
            Q0=makeQuery(id+"F51.imprint","IMPRINT",FACE,{"disambiguationData":[TD([[makeQuery(id+"F51.imprint","IMPRINT",EDGE,{"derivedFrom":sQuery(id+"F51.wireOp",EDGE,"E72")}),1.0]])]});
            var Q1;
            Q1=makeQuery(id+"F50.opExtrude","CAP_FACE",FACE,{"disambiguationData":[OSD([sQuery(id+"F49.wireOp",EDGE,"E71.bottom"),sQuery(id+"F49.wireOp",EDGE,"E71.top"),sQuery(id+"F49.wireOp",EDGE,"E71.left"),sQuery(id+"F49.wireOp",EDGE,"E71.right")])],"isStart":false});
            extrude(context, id + "F52", {"entities" : qUnion([Q0]), "operationType" : NewBodyOperationType.REMOVE, "endBound" : BoundingType.UP_TO_SURFACE, "oppositeDirection" : true, "depth" : 25.4 * mm, "endBoundEntityFace" : qUnion([Q1]), "offsetDistance" : 25.4 * mm});
        }
    });
